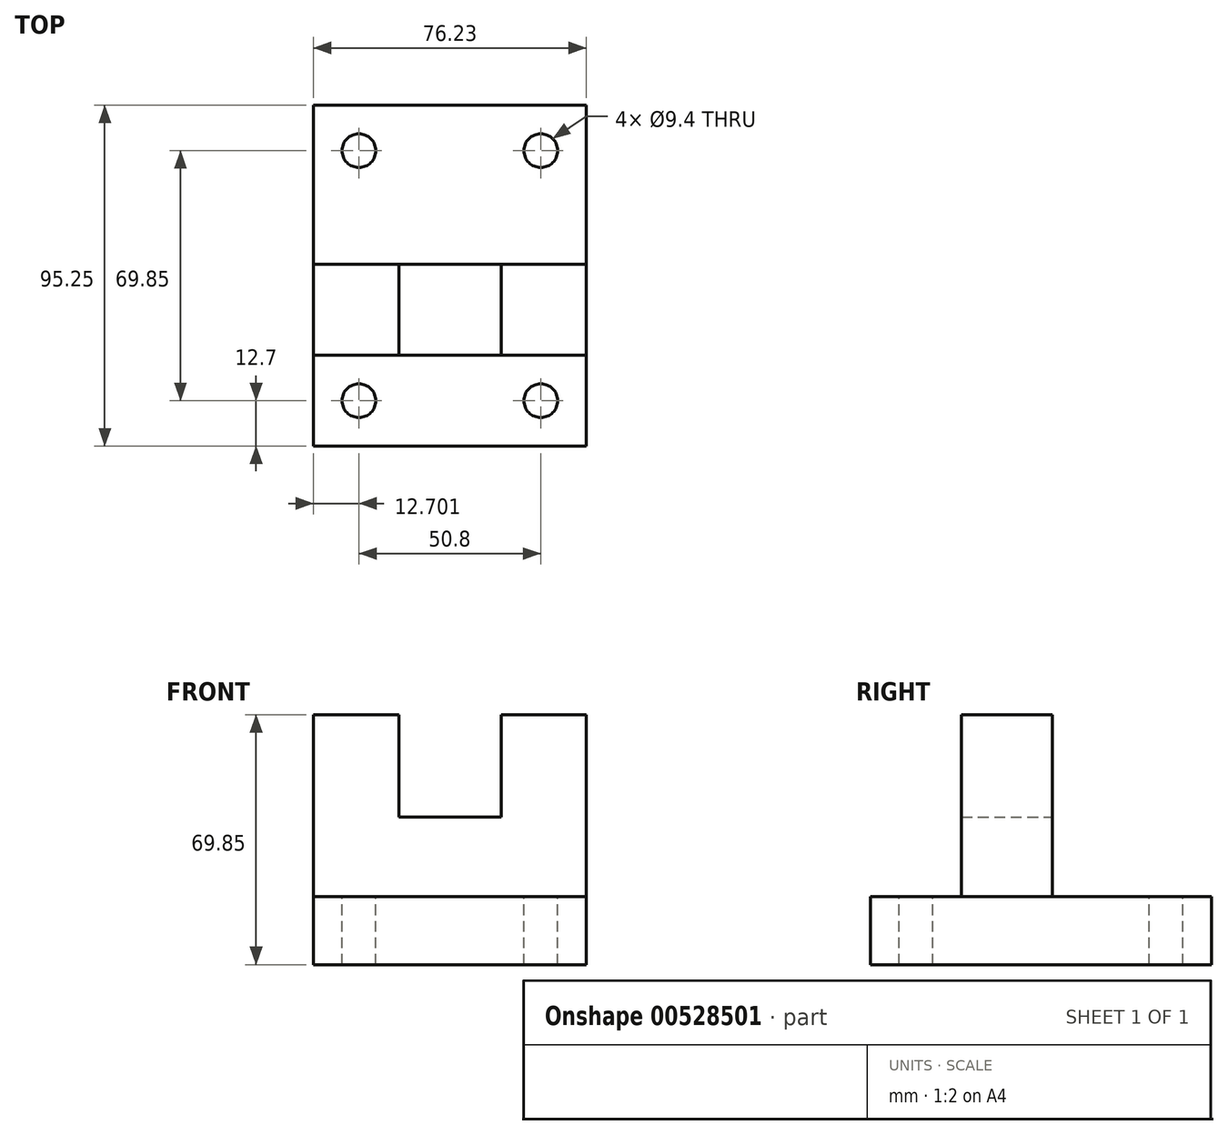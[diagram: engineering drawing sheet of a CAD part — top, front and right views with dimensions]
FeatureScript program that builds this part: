
annotation { "Feature Type Name" : "Feature", "Feature Type Description" : "" }
export const myFeature = defineFeature(function(context is Context, id is Id, definition is map)
    precondition{}
    {
        {
            var Q0;
            Q0=qCreatedBy(makeId("Front.planeOp"),FACE);
            var sketch = newSketch(context, id + "F0", { "sketchPlane" : qUnion([Q0])});
            skLineSegment(sketch, "E0", {"start": v(-60.18, 38.04) * mm, "end": v(-36.35, 38.04) * mm});
            skLineSegment(sketch, "E1", {"start": v(-36.35, 38.04) * mm, "end": v(-36.35, 9.46) * mm});
            skLineSegment(sketch, "E2", {"start": v(-36.35, 9.46) * mm, "end": v(-7.78, 9.46) * mm});
            skLineSegment(sketch, "E3", {"start": v(-7.78, 9.46) * mm, "end": v(-7.78, 38.04) * mm});
            skLineSegment(sketch, "E4", {"start": v(-7.78, 38.04) * mm, "end": v(16.05, 38.04) * mm});
            skLineSegment(sketch, "E5", {"start": v(16.05, 38.04) * mm, "end": v(16.05, -12.76) * mm});
            skLineSegment(sketch, "E6", {"start": v(16.05, -12.76) * mm, "end": v(-60.18, -12.76) * mm});
            skLineSegment(sketch, "E7", {"start": v(-60.18, -12.76) * mm, "end": v(-60.18, 38.04) * mm});
            skSolve(sketch);
        }
        {
            var Q0;
            Q0=makeQuery(id+"F0.imprint","IMPRINT",FACE,{"disambiguationData":[TD([[makeQuery(id+"F0.imprint","IMPRINT",EDGE,{"derivedFrom":sQuery(id+"F0.wireOp",EDGE,"E0")}),-1.0]])]});
            extrude(context, id + "F1", {"entities" : qUnion([Q0]), "depth" : 25.4 * mm, "offsetDistance" : 25.4 * mm});
        }
        {
            var Q0;
            Q0=makeQuery(id+"F1.opExtrude","SWEPT_FACE",FACE,{"disambiguationData":[OSD([sQuery(id+"F0.wireOp",EDGE,"E7")])]});
            var sketch = newSketch(context, id + "F2", { "sketchPlane" : qUnion([Q0])});
            skPoint(sketch, "E8.middle", {"position": v(26.39, -17) * mm});
            skPoint(sketch, "E8.right.end.orphan", {"position": v(131.95, -12.83) * mm});
            skPoint(sketch, "E8.right.start.orphan", {"position": v(131.95, -21.18) * mm});
            skPoint(sketch, "E8.left.end.orphan", {"position": v(-79.17, -12.83) * mm});
            skPoint(sketch, "E8.left.start.orphan", {"position": v(-79.17, -21.18) * mm});
            skLineSegment(sketch, "E9", {"start": v(0, -12.76) * mm, "end": v(-44.45, -12.76) * mm});
            skLineSegment(sketch, "E10", {"start": v(-44.45, -12.76) * mm, "end": v(-44.45, -31.81) * mm});
            skLineSegment(sketch, "E11", {"start": v(-44.45, -31.81) * mm, "end": v(50.8, -31.81) * mm});
            skLineSegment(sketch, "E12", {"start": v(50.8, -31.81) * mm, "end": v(50.8, -12.76) * mm});
            skLineSegment(sketch, "E13", {"start": v(50.8, -12.76) * mm, "end": v(0, -12.76) * mm});
            skPoint(sketch, "E14", {"position": v(25.4, -12.76) * mm});
            skSolve(sketch);
        }
        {
            var Q0;
            Q0 = qSketchRegion(id + "F2", true);
            extrude(context, id + "F3", {"entities" : qUnion([Q0]), "operationType" : NewBodyOperationType.ADD, "oppositeDirection" : true, "depth" : 76.2 * mm, "offsetDistance" : 25.4 * mm});
        }
        {
            var Q0;
            {var subQ1=sQuery(id+"F2.wireOp",EDGE,"E13");var subQ2=sQuery(id+"F2.wireOp",EDGE,"E12");var subQ5=sQuery(id+"F2.wireOp",EDGE,"E9");Q0=makeQuery(id+"F3.boolean.opBoolean","SPLIT",FACE,{"disambiguationData":[TD([makeQuery(id+"F3.opExtrude","SWEPT_FACE",FACE,{"disambiguationData":[OSD([subQ2])]})])],"derivedFrom":makeQuery(id+"F3.opExtrude","SWEPT_FACE",FACE,{"disambiguationData":[OSD([subQ5,subQ1])]})});}
            var sketch = newSketch(context, id + "F4", { "sketchPlane" : qUnion([Q0])});
            skLineSegment(sketch, "E15", {"start": v(16.02, 44.45) * mm, "end": v(16.02, 31.75) * mm});
            skLineSegment(sketch, "E16", {"start": v(16.02, 44.45) * mm, "end": v(3.32, 44.45) * mm});
            skCircle(sketch, "E17", {"center": v(3.32, 31.75) * mm, "radius": 4.7 * mm});
            skLineSegment(sketch, "E18", {"start": v(-60.18, 44.45) * mm, "end": v(-47.48, 44.45) * mm});
            skLineSegment(sketch, "E19", {"start": v(-60.18, 44.45) * mm, "end": v(-60.18, 31.75) * mm});
            skCircle(sketch, "E20", {"center": v(-47.48, 31.75) * mm, "radius": 4.7 * mm});
            skLineSegment(sketch, "E21", {"start": v(-60.18, -50.8) * mm, "end": v(-60.18, -38.1) * mm});
            skLineSegment(sketch, "E22", {"start": v(-60.18, -50.8) * mm, "end": v(-47.48, -50.8) * mm});
            skLineSegment(sketch, "E23", {"start": v(16.02, -50.8) * mm, "end": v(16.02, -38.1) * mm});
            skLineSegment(sketch, "E24", {"start": v(16.02, -50.8) * mm, "end": v(3.32, -50.8) * mm});
            skCircle(sketch, "E25", {"center": v(-47.48, -38.1) * mm, "radius": 4.7 * mm});
            skCircle(sketch, "E26", {"center": v(3.32, -38.1) * mm, "radius": 4.7 * mm});
            skSolve(sketch);
        }
        {
            var Q0;
            Q0 = qSketchRegion(id + "F4", true);
            extrude(context, id + "F5", {"entities" : qUnion([Q0]), "operationType" : NewBodyOperationType.REMOVE, "oppositeDirection" : true, "depth" : 25.4 * mm, "offsetDistance" : 25.4 * mm});
        }
    });
